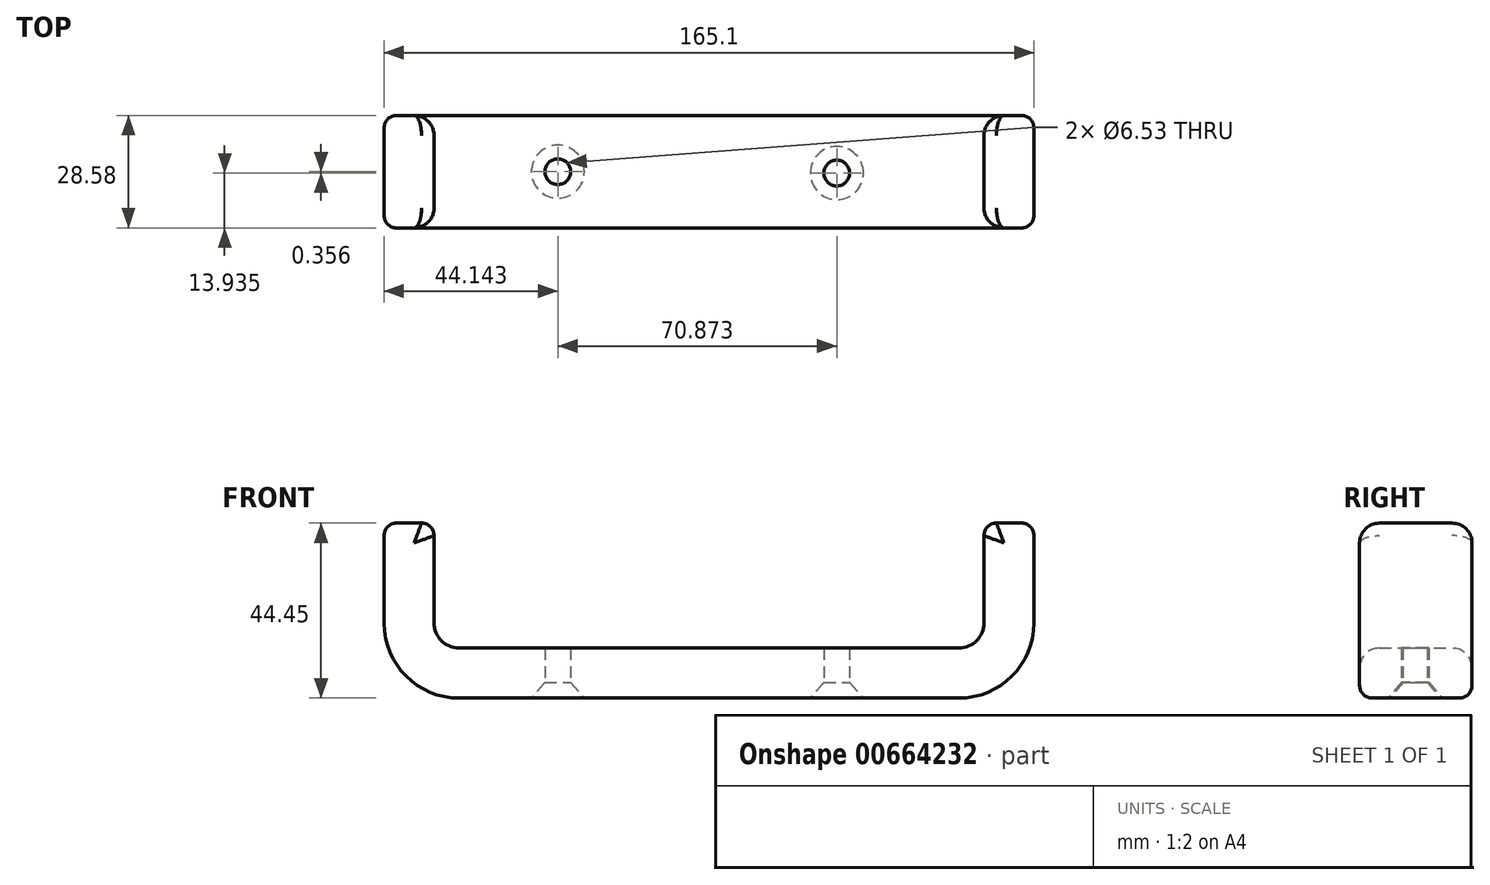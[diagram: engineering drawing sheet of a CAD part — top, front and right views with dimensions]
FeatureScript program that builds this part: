
annotation { "Feature Type Name" : "Feature", "Feature Type Description" : "" }
export const myFeature = defineFeature(function(context is Context, id is Id, definition is map)
    precondition{}
    {
        {
            var Q0;
            Q0=qCreatedBy(makeId("Front.planeOp"),FACE);
            var sketch = newSketch(context, id + "F0", { "sketchPlane" : qUnion([Q0])});
            skLineSegment(sketch, "E0", {"start": v(59.66, 0) * mm, "end": v(-67.34, 0) * mm});
            skArc(sketch, "E1", {"start": v(-67.34, 0) * mm, "mid": v(-80.81, 5.58) * mm, "end": v(-86.4, 19.05) * mm});
            skArc(sketch, "E2", {"start": v(59.66, 0) * mm, "mid": v(73.13, 5.58) * mm, "end": v(78.7, 19.05) * mm});
            skLineSegment(sketch, "E3", {"start": v(-86.4, 19.05) * mm, "end": v(-86.4, 44.45) * mm});
            skLineSegment(sketch, "E4", {"start": v(78.7, 19.05) * mm, "end": v(78.7, 44.45) * mm});
            skLineSegment(sketch, "E5.0", {"start": v(59.66, 12.7) * mm, "end": v(-67.34, 12.7) * mm});
            skLineSegment(sketch, "E6.0", {"start": v(66, 19.05) * mm, "end": v(66, 44.45) * mm});
            skLineSegment(sketch, "E6.1", {"start": v(-73.7, 19.05) * mm, "end": v(-73.7, 44.45) * mm});
            skArc(sketch, "E6.2", {"start": v(-67.34, 12.7) * mm, "mid": v(-71.83, 14.56) * mm, "end": v(-73.7, 19.05) * mm});
            skArc(sketch, "E6.4", {"start": v(59.66, 12.7) * mm, "mid": v(64.15, 14.56) * mm, "end": v(66, 19.05) * mm});
            skLineSegment(sketch, "E7", {"start": v(-73.7, 44.45) * mm, "end": v(-86.4, 44.45) * mm});
            skLineSegment(sketch, "E8", {"start": v(78.7, 44.45) * mm, "end": v(66, 44.45) * mm});
            skSolve(sketch);
        }
        {
            var Q0;
            Q0=makeQuery(id+"F0.imprint","IMPRINT",FACE,{"disambiguationData":[TD([[makeQuery(id+"F0.imprint","IMPRINT",EDGE,{"derivedFrom":sQuery(id+"F0.wireOp",EDGE,"E0")}),-1.0]])]});
            extrude(context, id + "F1", {"entities" : qUnion([Q0]), "depth" : 28.57 * mm, "offsetDistance" : 25.4 * mm});
        }
        {
            var Q0;
            Q0=makeQuery(id+"F1.opExtrude","SWEPT_FACE",FACE,{"disambiguationData":[OSD([sQuery(id+"F0.wireOp",EDGE,"E0")])]});
            var sketch = newSketch(context, id + "F2", { "sketchPlane" : qUnion([Q0])});
            skCircle(sketch, "E9", {"center": v(-42.25, 14.29) * mm, "radius": 6.35 * mm});
            skPoint(sketch, "E9.first.point", {"position": v(-46.38, 19.11) * mm});
            skPoint(sketch, "E9.second.point", {"position": v(-36.46, 11.68) * mm});
            skPoint(sketch, "E9.third.point", {"position": v(-42.18, 20.64) * mm});
            skCircle(sketch, "E10", {"center": v(28.63, 14.65) * mm, "radius": 6.35 * mm});
            skPoint(sketch, "E10.first.point", {"position": v(23.5, 18.4) * mm});
            skPoint(sketch, "E10.second.point", {"position": v(33.3, 10.35) * mm});
            skPoint(sketch, "E10.third.point", {"position": v(25.78, 20.32) * mm});
            skSolve(sketch);
        }
        {
            var Q0;
            Q0=sQuery(id+"F2.wireOp",VERTEX,"E9.center");
            var Q1;
            Q1=makeQuery(id+"F1.opExtrude","SWEPT_BODY",BODY,{"disambiguationData":[OSD([sQuery(id+"F0.wireOp",EDGE,"E0"),sQuery(id+"F0.wireOp",EDGE,"E1"),sQuery(id+"F0.wireOp",EDGE,"E2"),sQuery(id+"F0.wireOp",EDGE,"E3"),sQuery(id+"F0.wireOp",EDGE,"E4"),sQuery(id+"F0.wireOp",EDGE,"E6.0"),sQuery(id+"F0.wireOp",EDGE,"E6.1"),sQuery(id+"F0.wireOp",EDGE,"E6.2"),sQuery(id+"F0.wireOp",EDGE,"E5.0"),sQuery(id+"F0.wireOp",EDGE,"E6.4"),sQuery(id+"F0.wireOp",EDGE,"E7"),sQuery(id+"F0.wireOp",EDGE,"E8")])]});
            hole(context, id + "F3", {"style" : HoleStyle.C_SINK, "endStyle" : HoleEndStyle.THROUGH, "standardTappedOrClearance" : lookupTablePath({ "standard" : "ANSI", "fit" : "Close", "size" : "1/4", "type" : "Clearance" }), "standardBlindInLast" : lookupTablePath({ "fit" : "Close", "standard" : "ANSI", "size" : "1/4", "type" : "Clearance" }), "holeDiameter" : 6.53 * mm, "cSinkDiameter" : 13.5 * mm, "cSinkAngle" : 82 * degree, "majorDiameter" : 6.35 * mm, "isTappedThrough" : true, "tappedDepth" : 12.7 * mm, "tapClearance" : 3, "locations" : qUnion([Q0]), "scope" : qUnion([Q1])});
        }
        {
            var Q0;
            Q0=sQuery(id+"F2.wireOp",VERTEX,"E10.center");
            var Q1;
            Q1=makeQuery(id+"F1.opExtrude","SWEPT_BODY",BODY,{"disambiguationData":[OSD([sQuery(id+"F0.wireOp",EDGE,"E0"),sQuery(id+"F0.wireOp",EDGE,"E1"),sQuery(id+"F0.wireOp",EDGE,"E2"),sQuery(id+"F0.wireOp",EDGE,"E3"),sQuery(id+"F0.wireOp",EDGE,"E4"),sQuery(id+"F0.wireOp",EDGE,"E6.0"),sQuery(id+"F0.wireOp",EDGE,"E6.1"),sQuery(id+"F0.wireOp",EDGE,"E6.2"),sQuery(id+"F0.wireOp",EDGE,"E5.0"),sQuery(id+"F0.wireOp",EDGE,"E6.4"),sQuery(id+"F0.wireOp",EDGE,"E7"),sQuery(id+"F0.wireOp",EDGE,"E8")])]});
            hole(context, id + "F4", {"style" : HoleStyle.C_SINK, "endStyle" : HoleEndStyle.THROUGH, "standardTappedOrClearance" : lookupTablePath({ "standard" : "ANSI", "fit" : "Close", "size" : "1/4", "type" : "Clearance" }), "standardBlindInLast" : lookupTablePath({ "fit" : "Close", "standard" : "ANSI", "size" : "1/4", "type" : "Clearance" }), "holeDiameter" : 6.53 * mm, "cSinkDiameter" : 13.5 * mm, "cSinkAngle" : 82 * degree, "majorDiameter" : 6.35 * mm, "isTappedThrough" : true, "tappedDepth" : 12.7 * mm, "tapClearance" : 3, "locations" : qUnion([Q0]), "scope" : qUnion([Q1])});
        }
        {
            var Q0;
            Q0=makeQuery(id+"F1.opExtrude","SWEPT_EDGE",EDGE,{"disambiguationData":[OSD([sQuery(id+"F0.wireOp",EDGE,"E6.0"),sQuery(id+"F0.wireOp",EDGE,"E8")])]});
            var Q1;
            Q1=makeQuery(id+"F1.opExtrude","SWEPT_EDGE",EDGE,{"disambiguationData":[OSD([sQuery(id+"F0.wireOp",EDGE,"E4"),sQuery(id+"F0.wireOp",EDGE,"E8")])]});
            var Q2;
            Q2=makeQuery(id+"F1.opExtrude","SWEPT_EDGE",EDGE,{"disambiguationData":[OSD([sQuery(id+"F0.wireOp",EDGE,"E3"),sQuery(id+"F0.wireOp",EDGE,"E7")])]});
            var Q3;
            Q3=makeQuery(id+"F1.opExtrude","SWEPT_EDGE",EDGE,{"disambiguationData":[OSD([sQuery(id+"F0.wireOp",EDGE,"E6.1"),sQuery(id+"F0.wireOp",EDGE,"E7")])]});
            var Q4;
            Q4=makeQuery(id+"F1.opExtrude","CAP_EDGE",EDGE,{"disambiguationData":[OSD([sQuery(id+"F0.wireOp",EDGE,"E0")])],"isStart":true});
            var Q5;
            Q5=makeQuery(id+"F1.opExtrude","CAP_EDGE",EDGE,{"disambiguationData":[OSD([sQuery(id+"F0.wireOp",EDGE,"E0")])],"isStart":false});
            fillet(context, id + "F5", {"entities" : qUnion([Q0, Q1, Q2, Q3, Q4, Q5]), "radius" : 3.17 * mm, "tangentPropagation" : true, "allowEdgeOverflow" : false});
        }
        {
            var Q0;
            Q0=makeQuery(id+"F1.opExtrude","CAP_EDGE",EDGE,{"disambiguationData":[OSD([sQuery(id+"F0.wireOp",EDGE,"E7")])],"isStart":true});
            var Q1;
            Q1=makeQuery(id+"F1.opExtrude","CAP_EDGE",EDGE,{"disambiguationData":[OSD([sQuery(id+"F0.wireOp",EDGE,"E7")])],"isStart":false});
            fillet(context, id + "F6", {"entities" : qUnion([Q0, Q1]), "radius" : 5.08 * mm, "tangentPropagation" : true, "allowEdgeOverflow" : false});
        }
    });
